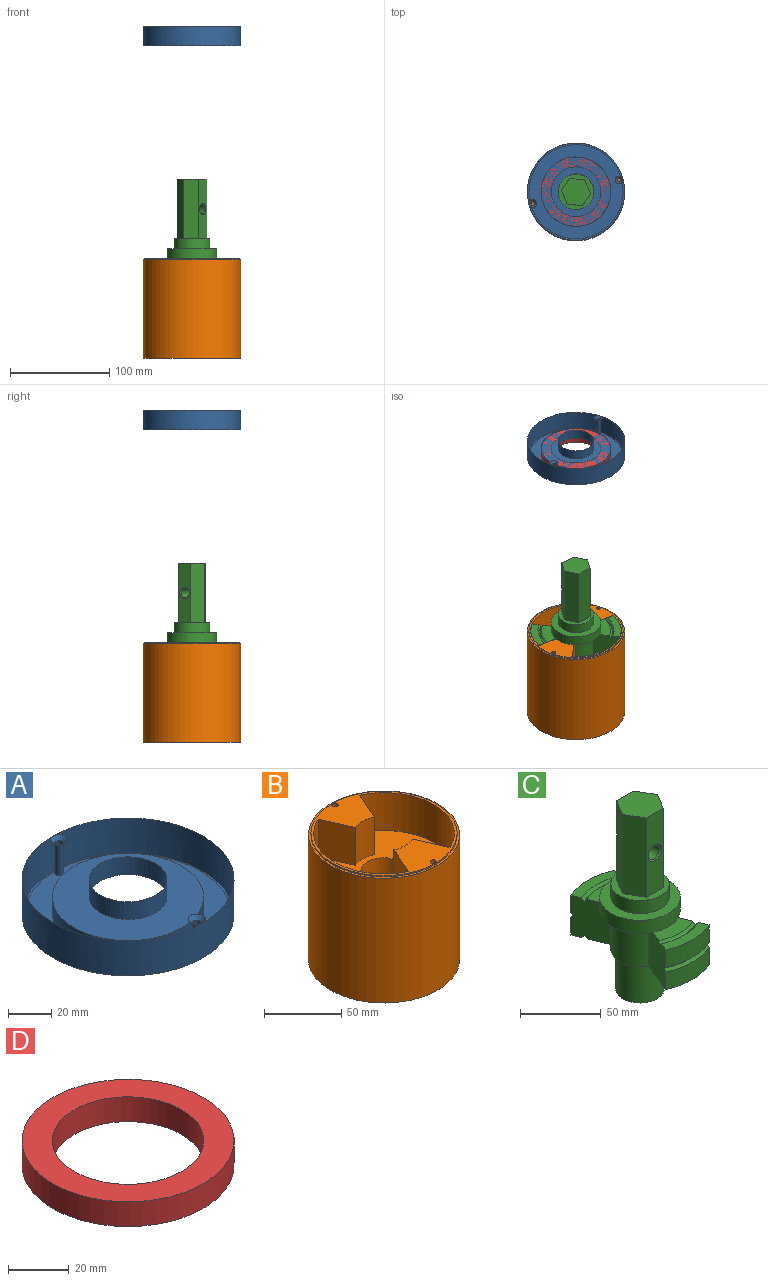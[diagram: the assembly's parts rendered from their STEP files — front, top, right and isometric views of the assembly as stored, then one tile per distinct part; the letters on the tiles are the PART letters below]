
ASSEMBLY  parts=4 mates=7
PART A: 12 faces, bbox 98x98x20 mm
  f0: cylinder r=2mm len=17mm, axis (0,0,-1), area 213.6mm2, adj f6,f10
  f1: cylinder r=49mm len=98mm, axis (0,0,-1), area 6157.5mm2, adj f3,f4
  f2: cylinder r=2mm len=17mm, axis (0,0,-1), area 213.6mm2, adj f6,f11
  f3: plane 98x98mm, normal (0,0,1), area 6424.6mm2, adj f1,f9,f10,f11
  f4: plane 98x98mm, normal (0,0,-1), area 484.6mm2, adj f1,f5
  f5: cylinder r=47.4mm len=94.8mm, axis (0,0,-1), area 297.8mm2, adj f4,f6
  f6: plane 94.8x94.8mm, normal (0,0,-1), area 3184.8mm2, adj f0,f2,f5,f7
  f7: cylinder r=35mm len=70mm, axis (0,0,-1), area 1979.2mm2, adj f6,f8
  f8: plane 70x70mm, normal (0,0,-1), area 2830.6mm2, adj f7,f9
  f9: cylinder r=18mm len=36mm, axis (0,0,-1), area 1131mm2, adj f3,f8
  f10: cone r=2mm half-angle=45deg, axis (0,0,1), area 53.3mm2, adj f0,f3
  f11: cone r=2mm half-angle=45deg, axis (0,0,1), area 53.3mm2, adj f2,f3
PART B: 27 faces, bbox 98x98x100 mm
  f0: cylinder r=49mm len=99mm, axis (0,0,1), area 30479.7mm2, adj f1,f3
  f1: plane 98x98mm, normal (0,0,-1), area 6958.4mm2, adj f0,f20,f21,f22,f23,f24,f25
  f2: cylinder r=47.4mm len=94.8mm, axis (0,0,1), area 297.8mm2, adj f3,f4
  f3: plane 98x98mm, normal (0,0,1), area 484.6mm2, adj f0,f2
  f4: plane 94.8x94.8mm, normal (0,0,1), area 1982.9mm2, adj f2,f5,f6,f7,f8,f9,f10,f11
  f5: cylinder r=19.5mm len=30mm, axis (0,0,1), area 527.7mm2, adj f4,f6,f12,f13
  f6: plane 30x23.9mm, normal (0.92,0.4,0), area 783.2mm2, adj f4,f5,f7,f13
  f7: cylinder r=45.6mm len=82.91mm, axis (0,0,1), area 3121.8mm2, adj f4,f6,f8,f13
  f8: plane 30x23.9mm, normal (0.92,-0.4,0), area 783.2mm2, adj f4,f7,f9,f13
  f9: cylinder r=19.5mm len=30mm, axis (0,0,1), area 527.7mm2, adj f4,f8,f10,f13
  f10: plane 30x23.9mm, normal (-0.92,-0.4,0), area 783.2mm2, adj f4,f9,f11,f13
  f11: cylinder r=45.6mm len=82.91mm, axis (0,0,1), area 3121.8mm2, adj f4,f10,f12,f13
  f12: plane 30x23.9mm, normal (-0.92,0.4,0), area 783.2mm2, adj f4,f5,f11,f13
  f13: plane 91.2x82.91mm, normal (0,0,1), area 4343.5mm2, adj f5,f6,f7,f8,f9,f10,f11,f12
  f14: cylinder r=15mm len=30mm, axis (0,0,1), area 2827.4mm2, adj f13,f15
  f15: plane 30x30mm, normal (0,0,1), area 706.9mm2, adj f14
  f16: cylinder r=2mm len=10mm, axis (0,0,1), area 125.7mm2, adj f4,f17
  f17: plane 4x4mm, normal (0,0,1), area 12.6mm2, adj f16
  f18: cylinder r=2mm len=10mm, axis (0,0,1), area 125.7mm2, adj f4,f19
  f19: plane 4x4mm, normal (0,0,1), area 12.6mm2, adj f18
  f20: plane 30x15mm, normal (-0.02,1,0), area 450mm2, adj f1,f21,f25,f26
  f21: plane 30x12.87mm, normal (0.86,0.51,0), area 450mm2, adj f1,f20,f22,f26
  f22: plane 30x13.11mm, normal (0.87,-0.49,0), area 450mm2, adj f1,f21,f23,f26
  f23: plane 30x15mm, normal (0.02,-1,0), area 450mm2, adj f1,f22,f24,f26
  f24: plane 30x12.87mm, normal (-0.86,-0.51,0), area 450mm2, adj f1,f23,f25,f26
  f25: plane 30x13.11mm, normal (-0.87,0.49,0), area 450mm2, adj f1,f20,f24,f26
  f26: plane 30x26.22mm, normal (0,0,-1), area 584.6mm2, adj f20,f21,f22,f23,f24,f25
PART C: 47 faces, bbox 50x91x139.7 mm
  f0: plane 36x36mm, normal (0,0,1), area 433.3mm2, adj f36,f37,f38,f39,f40,f41,f42
  f1: cylinder r=15mm len=30mm, axis (0,0,1), area 2799.2mm2, adj f2,f5
  f2: plane 30x30mm, normal (0,0,-1), area 706.9mm2, adj f1
  f3: cylinder r=18mm len=31.73mm, axis (0,0,-1), area 1165.3mm2, adj f5,f7,f19,f23
  f4: cylinder r=18mm len=31.73mm, axis (0,0,-1), area 1165.3mm2, adj f5,f9,f21,f35
  f5: plane 69.4x36mm, normal (0,0,-1), area 1120.3mm2, adj f1,f3,f4,f7,f9,f18,f21,f23
  f6: plane 29.76x12.34mm, normal (0,0,1), area 261.6mm2, adj f7,f9,f16,f33
  f7: plane 30x25.48mm, normal (0.92,-0.38,0), area 816.9mm2, adj f3,f5,f6,f8,f10,f11,f12,f13
  f8: cylinder r=45.5mm len=38mm, axis (0,0,-1), area 517.5mm2, adj f7,f9,f10,f14
  f9: plane 30x25.48mm, normal (-0.92,-0.38,0), area 816.9mm2, adj f4,f5,f6,f8,f10,f11,f12,f13
  f10: plane 38x10.82mm, normal (0,0,1), area 262mm2, adj f7,f8,f9,f15
  f11: plane 38x10.82mm, normal (0,0,-1), area 262mm2, adj f7,f9,f12,f17
  f12: cylinder r=45.5mm len=38mm, axis (0,0,-1), area 517.5mm2, adj f7,f9,f11,f13
  f13: cone r=43.7mm half-angle=45deg, axis (0,0,-1), area 98mm2, adj f7,f9,f12,f14
  f14: cone r=45.5mm half-angle=45deg, axis (0,0,1), area 98mm2, adj f7,f8,f9,f13
  f15: cone r=38.3mm half-angle=45deg, axis (0,0,1), area 83.7mm2, adj f7,f9,f10,f16
  f16: cone r=36.5mm half-angle=45deg, axis (0,0,-1), area 80.1mm2, adj f6,f7,f9,f15
  f17: cone r=38.3mm half-angle=45deg, axis (0,0,-1), area 83.7mm2, adj f7,f9,f11,f18
  f18: cone r=36.5mm half-angle=45deg, axis (0,0,1), area 80.1mm2, adj f5,f7,f9,f17
  f19: plane 44.72x16.5mm, normal (0,0,-1), area 329.7mm2, adj f3,f7,f23,f33
  f20: plane 29.76x12.34mm, normal (0,0,1), area 261.6mm2, adj f21,f23,f30,f33
  f21: plane 30x25.48mm, normal (-0.92,0.38,0), area 816.9mm2, adj f4,f5,f20,f22,f24,f25,f26,f27
  f22: cylinder r=45.5mm len=38mm, axis (0,0,-1), area 517.5mm2, adj f21,f23,f24,f28
  f23: plane 30x25.48mm, normal (0.92,0.38,0), area 816.9mm2, adj f3,f5,f19,f20,f22,f24,f25,f26
  f24: plane 38x10.82mm, normal (0,0,1), area 262mm2, adj f21,f22,f23,f29
  f25: plane 38x10.82mm, normal (0,0,-1), area 262mm2, adj f21,f23,f26,f31
  f26: cylinder r=45.5mm len=38mm, axis (0,0,-1), area 517.5mm2, adj f21,f23,f25,f27
  f27: cone r=43.7mm half-angle=45deg, axis (0,0,-1), area 98mm2, adj f21,f23,f26,f28
  f28: cone r=45.5mm half-angle=45deg, axis (0,0,1), area 98mm2, adj f21,f22,f23,f27
  f29: cone r=38.3mm half-angle=45deg, axis (0,0,1), area 83.7mm2, adj f21,f23,f24,f30
  f30: cone r=36.5mm half-angle=45deg, axis (0,0,-1), area 80.1mm2, adj f20,f21,f23,f29
  f31: cone r=38.3mm half-angle=45deg, axis (0,0,-1), area 83.7mm2, adj f21,f23,f25,f32
  f32: cone r=36.5mm half-angle=45deg, axis (0,0,1), area 80.1mm2, adj f5,f21,f23,f31
  f33: cylinder r=25mm len=50mm, axis (0,0,-1), area 1570.8mm2, adj f6,f19,f20,f34,f35
  f34: plane 50x50mm, normal (0,0,1), area 945.6mm2, adj f33,f36
  f35: plane 44.72x16.5mm, normal (0,0,-1), area 329.7mm2, adj f4,f9,f21,f33
  f36: cylinder r=18mm len=36mm, axis (0,0,-1), area 1131mm2, adj f0,f34
  f37: plane 60x15mm, normal (0,-1,0), area 786.9mm2, adj f0,f38,f42,f43,f45
  f38: plane 60x12.99mm, normal (0.87,-0.5,0), area 900mm2, adj f0,f37,f39,f43
  f39: plane 60x12.99mm, normal (0.87,0.5,0), area 900mm2, adj f0,f38,f40,f43
  f40: plane 60x15mm, normal (0,1,0), area 786.9mm2, adj f0,f39,f41,f43,f46
  f41: plane 60x12.99mm, normal (-0.87,0.5,0), area 900mm2, adj f0,f40,f42,f43
  f42: plane 60x12.99mm, normal (-0.87,-0.5,0), area 900mm2, adj f0,f37,f41,f43
  f43: plane 30x25.98mm, normal (0,0,1), area 584.6mm2, adj f37,f38,f39,f40,f41,f42
  f44: cylinder r=5mm len=23.98mm, axis (0,-1,0), area 753.4mm2, adj f45,f46
  f45: cone r=5mm half-angle=45deg, axis (0,-1,0), area 48.9mm2, adj f37,f44
  f46: cone r=6mm half-angle=45deg, axis (0,1,0), area 48.9mm2, adj f40,f44
PART D: 4 faces, bbox 70x70x10 mm
  f0: cylinder r=25mm len=50mm, axis (0,0,-1), area 1570.8mm2, adj f2,f3
  f1: cylinder r=35mm len=70mm, axis (0,0,-1), area 2199.1mm2, adj f2,f3
  f2: plane 70x70mm, normal (0,0,1), area 1885mm2, adj f0,f1
  f3: plane 70x70mm, normal (0,0,-1), area 1885mm2, adj f0,f1
PLACE A rot(axis=(0,0,1),105.2deg) t=(18.21,8.12,214.18)mm
PLACE B rot(axis=(0,0,-1),74.8deg) t=(18.21,8.12,0)mm fixed
PLACE C rot(axis=(0,0,1),55.2deg) t=(18.21,8.12,-30)mm
PLACE D rot(axis=(0,0,1),15.2deg) t=(18.21,8.12,214.18)mm
MATE planar D.f1 <-> A.f5  axis (0,0,1) through (18.21,8.12,224.18)mm
MATE parallel A.f1 <-> B.f7  axis (0,0,-1) through (18.21,8.12,214.18)mm
MATE cylindrical A.f2 <-> B.f18  axis (0,0,1) through (61.64,19.88,232.18)mm
MATE cylindrical C.f1 <-> B.f14  axis (0,0,-1) through (18.21,8.12,-59.7)mm
MATE planar C.f35 <-> B.f9  axis (0,0,-1) through (8.14,-6.34,0)mm
MATE slider D.f0 <-> A.f9  axis (0,0,1) through (18.21,8.12,224.18)mm
MATE cylindrical A.f0 <-> B.f16  axis (0,0,1) through (-25.23,-3.65,234.18)mm
